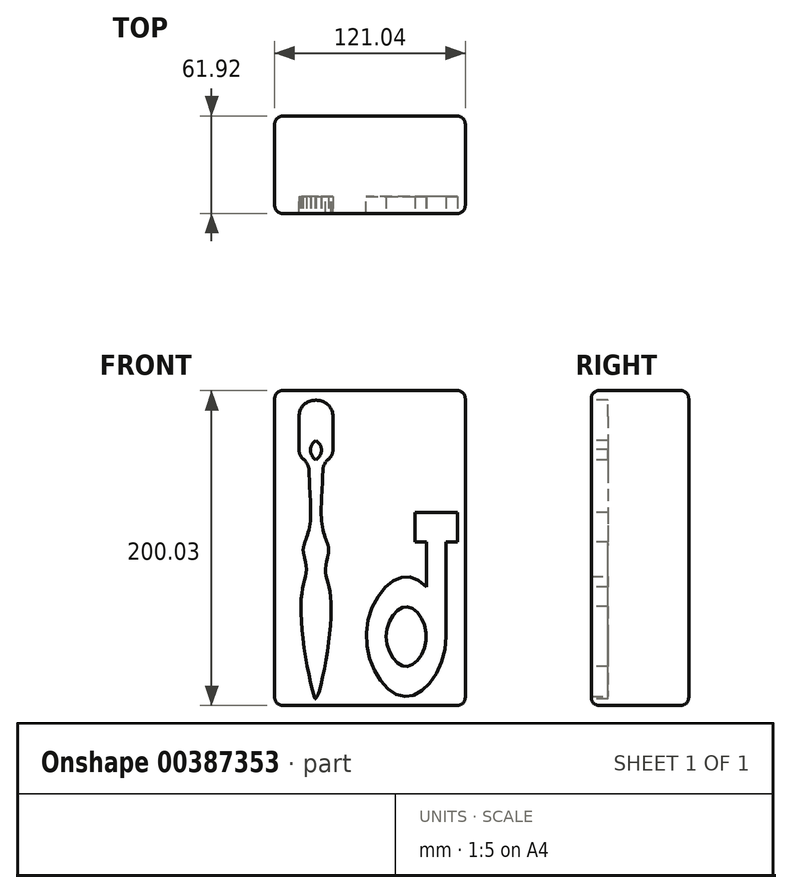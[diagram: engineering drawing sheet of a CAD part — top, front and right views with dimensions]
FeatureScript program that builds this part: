
annotation { "Feature Type Name" : "Feature", "Feature Type Description" : "" }
export const myFeature = defineFeature(function(context is Context, id is Id, definition is map)
    precondition{}
    {
        {
            var Q0;
            Q0=qCreatedBy(makeId("Top.planeOp"),FACE);
            var sketch = newSketch(context, id + "F0", { "sketchPlane" : qUnion([Q0])});
            skLineSegment(sketch, "E0.bottom", {"start": v(60.52, -30.96) * mm, "end": v(-60.52, -30.96) * mm});
            skLineSegment(sketch, "E0.top", {"start": v(60.52, 30.96) * mm, "end": v(-60.52, 30.96) * mm});
            skLineSegment(sketch, "E0.left", {"start": v(60.52, -30.96) * mm, "end": v(60.52, 30.96) * mm});
            skLineSegment(sketch, "E0.right", {"start": v(-60.52, -30.96) * mm, "end": v(-60.52, 30.96) * mm});
            skPoint(sketch, "E0.middle", {"position": v(0, 0) * mm});
            skSolve(sketch);
        }
        {
            var Q0;
            Q0=makeQuery(id+"F0.imprint","IMPRINT",FACE,{"disambiguationData":[TD([[makeQuery(id+"F0.imprint","IMPRINT",EDGE,{"derivedFrom":sQuery(id+"F0.wireOp",EDGE,"E0.bottom")}),-1.0]])]});
            extrude(context, id + "F1", {"entities" : qUnion([Q0]), "depth" : 200.02 * mm});
        }
        {
            var Q0;
            Q0=makeQuery(id+"F1.opExtrude","SWEPT_EDGE",EDGE,{"disambiguationData":[OSD([sQuery(id+"F0.wireOp",EDGE,"E0.top"),sQuery(id+"F0.wireOp",EDGE,"E0.left")])]});
            var Q1;
            Q1=makeQuery(id+"F1.opExtrude","SWEPT_EDGE",EDGE,{"disambiguationData":[OSD([sQuery(id+"F0.wireOp",EDGE,"E0.top"),sQuery(id+"F0.wireOp",EDGE,"E0.right")])]});
            var Q2;
            Q2=makeQuery(id+"F1.opExtrude","CAP_EDGE",EDGE,{"disambiguationData":[OSD([sQuery(id+"F0.wireOp",EDGE,"E0.top")])],"isStart":false});
            var Q3;
            Q3=makeQuery(id+"F1.opExtrude","CAP_EDGE",EDGE,{"disambiguationData":[OSD([sQuery(id+"F0.wireOp",EDGE,"E0.top")])],"isStart":true});
            var Q4;
            Q4=makeQuery(id+"F1.opExtrude","CAP_EDGE",EDGE,{"disambiguationData":[OSD([sQuery(id+"F0.wireOp",EDGE,"E0.right")])],"isStart":true});
            var Q5;
            Q5=makeQuery(id+"F1.opExtrude","CAP_EDGE",EDGE,{"disambiguationData":[OSD([sQuery(id+"F0.wireOp",EDGE,"E0.bottom")])],"isStart":true});
            var Q6;
            Q6=makeQuery(id+"F1.opExtrude","CAP_EDGE",EDGE,{"disambiguationData":[OSD([sQuery(id+"F0.wireOp",EDGE,"E0.left")])],"isStart":true});
            var Q7;
            Q7=makeQuery(id+"F1.opExtrude","SWEPT_EDGE",EDGE,{"disambiguationData":[OSD([sQuery(id+"F0.wireOp",EDGE,"E0.bottom"),sQuery(id+"F0.wireOp",EDGE,"E0.right")])]});
            var Q8;
            Q8=makeQuery(id+"F1.opExtrude","CAP_EDGE",EDGE,{"disambiguationData":[OSD([sQuery(id+"F0.wireOp",EDGE,"E0.right")])],"isStart":false});
            var Q9;
            Q9=makeQuery(id+"F1.opExtrude","CAP_EDGE",EDGE,{"disambiguationData":[OSD([sQuery(id+"F0.wireOp",EDGE,"E0.bottom")])],"isStart":false});
            var Q10;
            Q10=makeQuery(id+"F1.opExtrude","CAP_EDGE",EDGE,{"disambiguationData":[OSD([sQuery(id+"F0.wireOp",EDGE,"E0.left")])],"isStart":false});
            var Q11;
            Q11=makeQuery(id+"F1.opExtrude","SWEPT_EDGE",EDGE,{"disambiguationData":[OSD([sQuery(id+"F0.wireOp",EDGE,"E0.bottom"),sQuery(id+"F0.wireOp",EDGE,"E0.left")])]});
            fillet(context, id + "F2", {"entities" : qUnion([Q0, Q1, Q2, Q3, Q4, Q5, Q6, Q7, Q8, Q9, Q10, Q11]), "radius" : 5.08 * mm, "tangentPropagation" : true, "allowEdgeOverflow" : false});
        }
        {
            var Q0;
            Q0=makeQuery(id+"F1.opExtrude","SWEPT_FACE",FACE,{"disambiguationData":[OSD([sQuery(id+"F0.wireOp",EDGE,"E0.bottom")])]});
            var sketch = newSketch(context, id + "F3", { "sketchPlane" : qUnion([Q0])});
            skLineSegment(sketch, "E1", {"start": v(22.99, 43.76) * mm, "end": v(22.99, 81.86) * mm, "construction": true});
            skLineSegment(sketch, "E2", {"start": v(22.99, 43.76) * mm, "end": v(22.99, 5.66) * mm, "construction": true});
            skLineSegment(sketch, "E3", {"start": v(22.99, 43.76) * mm, "end": v(48.39, 43.76) * mm, "construction": true});
            skLineSegment(sketch, "E4", {"start": v(22.99, 43.76) * mm, "end": v(-2.41, 43.76) * mm, "construction": true});
            skFitSpline(sketch, "E5", {"points": [v(22.99, 5.66) * mm, v(-2.41, 43.76) * mm, v(22.99, 81.86) * mm, v(48.39, 43.76) * mm, v(22.99, 5.66) * mm]});
            skLineSegment(sketch, "E6", {"start": v(48.39, 43.76) * mm, "end": v(48.39, 103.81) * mm});
            skLineSegment(sketch, "E7", {"start": v(36, 75.46) * mm, "end": v(36, 103.81) * mm});
            skLineSegment(sketch, "E8", {"start": v(48.39, 103.81) * mm, "end": v(55.44, 103.81) * mm});
            skLineSegment(sketch, "E9", {"start": v(55.44, 103.81) * mm, "end": v(55.44, 122.75) * mm});
            skLineSegment(sketch, "E10", {"start": v(55.44, 122.75) * mm, "end": v(28.53, 122.75) * mm});
            skLineSegment(sketch, "E11", {"start": v(28.53, 122.75) * mm, "end": v(28.53, 103.81) * mm});
            skLineSegment(sketch, "E12", {"start": v(28.53, 103.81) * mm, "end": v(36, 103.81) * mm});
            skFitSpline(sketch, "E13", {"points": [v(10.29, 43.76) * mm, v(22.99, 62.8) * mm, v(35.69, 43.76) * mm, v(22.99, 24.7) * mm, v(10.29, 43.76) * mm]});
            skSolve(sketch);
        }
        {
            var Q0;
            Q0=makeQuery(id+"F3.imprint","IMPRINT",FACE,{"disambiguationData":[TD([[makeQuery(id+"F3.imprint","IMPRINT",EDGE,{"derivedFrom":sQuery(id+"F3.wireOp",EDGE,"E5")}),-1.0]])]});
            var sketch = newSketch(context, id + "F4", { "sketchPlane" : qUnion([Q0])});
            skLineSegment(sketch, "E14.left", {"start": v(-45.06, 189.74) * mm, "end": v(-45.06, 162.78) * mm});
            skLineSegment(sketch, "E15", {"start": v(-34.31, 195) * mm, "end": v(-34.31, 0) * mm, "construction": true});
            skPoint(sketch, "E16", {"position": v(-34.31, 166.9) * mm});
            skArc(sketch, "E17", {"start": v(-34.31, 193.9) * mm, "mid": v(-40.08, 192.83) * mm, "end": v(-45.06, 189.74) * mm});
            skPoint(sketch, "E18", {"position": v(-45.06, 189.74) * mm});
            skPoint(sketch, "E19", {"position": v(-23.56, 189.74) * mm});
            skPoint(sketch, "E20", {"position": v(-80.03, 214.85) * mm});
            skPoint(sketch, "E14.bottom.start.orphan", {"position": v(-45.06, 195) * mm});
            skArc(sketch, "E21", {"start": v(-45.06, 162.78) * mm, "mid": v(-33.6, 156.6) * mm, "end": v(-36.72, 169.25) * mm});
            skPoint(sketch, "E22.orphan", {"position": v(-45.06, 166.9) * mm});
            skPoint(sketch, "E23.orphan", {"position": v(-23.56, 166.9) * mm});
            skPoint(sketch, "E24.orphan", {"position": v(-23.56, 195) * mm});
            skLineSegment(sketch, "E25", {"start": v(-42.7, 98.32) * mm, "end": v(-42.7, 98.32) * mm});
            skLineSegment(sketch, "E26", {"start": v(-26.06, 67.88) * mm, "end": v(-26.06, 67.88) * mm});
            skFitSpline(sketch, "E27.MirrorCS", {"points": [v(-34.88, 4.14) * mm, v(-43.7, 67.88) * mm, v(-40.42, 85.52) * mm, v(-42.7, 98.32) * mm], "startDerivative": vector(-31.6, 98.95) * mm, "endDerivative": vector(-13.68, 49.84) * mm});
            skFitSpline(sketch, "E28", {"points": [v(-36.72, 169.25) * mm, v(-37.97, 116.35) * mm, v(-42.7, 98.32) * mm], "startDerivative": vector(-21.47, -88.4) * mm, "endDerivative": vector(-3.98, -35.27) * mm});
            skLineSegment(sketch, "E29.trimOffspring", {"start": v(-40.19, 26.46) * mm, "end": v(-40.19, 26.46) * mm});
            skPoint(sketch, "E30.orphan", {"position": v(-40.42, 4.14) * mm});
            skPoint(sketch, "E31.end.orphan", {"position": v(-28.2, 4.14) * mm});
            skLineSegment(sketch, "E32.trimOffspring", {"start": v(-43.7, 67.88) * mm, "end": v(-43.7, 67.88) * mm});
            skPoint(sketch, "E14.right.end.orphan", {"position": v(-23.56, 162.78) * mm});
            skFitSpline(sketch, "E33.MirrorCS", {"points": [v(-33.74, 4.14) * mm, v(-24.92, 67.88) * mm, v(-28.2, 85.52) * mm, v(-25.93, 98.32) * mm], "startDerivative": vector(31.6, 98.95) * mm, "endDerivative": vector(13.68, 49.84) * mm});
            skFitSpline(sketch, "E34.MirrorCS", {"points": [v(-31.9, 169.25) * mm, v(-30.65, 116.35) * mm, v(-25.93, 98.32) * mm], "startDerivative": vector(21.47, -88.4) * mm, "endDerivative": vector(3.98, -35.27) * mm});
            skArc(sketch, "E35.MirrorCS", {"start": v(-23.56, 162.78) * mm, "mid": v(-35.03, 156.6) * mm, "end": v(-31.9, 169.25) * mm});
            skArc(sketch, "E36.MirrorCS", {"start": v(-34.31, 193.9) * mm, "mid": v(-28.55, 192.83) * mm, "end": v(-23.56, 189.74) * mm});
            skLineSegment(sketch, "E37.MirrorCS", {"start": v(-23.56, 189.74) * mm, "end": v(-23.56, 162.78) * mm});
            skArc(sketch, "E38.trimOffspring", {"start": v(-34.31, 168.36) * mm, "mid": v(-35.48, 168.92) * mm, "end": v(-36.72, 169.25) * mm});
            skArc(sketch, "E39.trimOffspring", {"start": v(-34.31, 168.36) * mm, "mid": v(-33.15, 168.92) * mm, "end": v(-31.9, 169.25) * mm});
            skArc(sketch, "E40.trimOffspring", {"start": v(-34.31, 156.12) * mm, "mid": v(-30.95, 163.52) * mm, "end": v(-36.72, 169.25) * mm});
            skPoint(sketch, "E41", {"position": v(-38.64, 155.04) * mm});
            skPoint(sketch, "E42", {"position": v(-34.31, 3.07) * mm});
            skLineSegment(sketch, "E43", {"start": v(-34.88, 4.14) * mm, "end": v(-33.74, 4.14) * mm});
            skSolve(sketch);
        }
        {
            var Q0;
            Q0 = qSketchRegion(id + "F4", true);
            var Q1;
            {var subQ0=sQuery(id+"F4.wireOp",EDGE,"E40.trimOffspring");var subQ1=sQuery(id+"F4.wireOp",EDGE,"E35.MirrorCS");var subQ2=makeQuery(id+"F4.imprint","INTERSECT",VERTEX,{"derivedFrom":[sQuery(id+"F4.wireOp",EDGE,"E21"),subQ1,subQ0]});Q1=makeQuery(id+"F4.imprint","IMPRINT",FACE,{"disambiguationData":[TD([[makeQuery(id+"F4.imprint","IMPRINT",EDGE,{"disambiguationData":[TD([[subQ2,-1.0]])],"derivedFrom":subQ1}),-1.0]])]});}
            var Q2;
            Q2 = qSketchRegion(id + "F3", true);
            var Q3;
            Q3=sQuery(id+"F4.wireOp",EDGE,"E34.MirrorCS");
            var Q4;
            Q4=sQuery(id+"F4.wireOp",EDGE,"E28");
            var Q5;
            Q5=sQuery(id+"F4.wireOp",EDGE,"E27.MirrorCS");
            var Q6;
            Q6=sQuery(id+"F4.wireOp",EDGE,"E33.MirrorCS");
            var Q7;
            Q7=sQuery(id+"F4.wireOp",EDGE,"E37.MirrorCS");
            var Q8;
            Q8=sQuery(id+"F4.wireOp",EDGE,"E35.MirrorCS");
            var Q9;
            Q9=sQuery(id+"F4.wireOp",EDGE,"E21");
            var Q10;
            Q10=sQuery(id+"F4.wireOp",EDGE,"E14.left");
            var Q11;
            Q11=sQuery(id+"F4.wireOp",EDGE,"E17");
            var Q12;
            Q12=sQuery(id+"F4.wireOp",EDGE,"E36.MirrorCS");
            extrude(context, id + "F5", {"entities" : qUnion([Q0, Q1, Q2]), "operationType" : NewBodyOperationType.REMOVE, "surfaceEntities" : qUnion([Q3, Q4, Q5, Q6, Q7, Q8, Q9, Q10, Q11, Q12]), "oppositeDirection" : true, "depth" : 10.67 * mm});
        }
        {
            var Q0;
            Q0=makeQuery(id+"F5.boolean.opBoolean","COPY",EDGE,{"derivedFrom":makeQuery(id+"F5.opExtrude","SWEPT_EDGE",EDGE,{"disambiguationData":[OSD([sQuery(id+"F4.wireOp",EDGE,"E36.MirrorCS"),sQuery(id+"F4.wireOp",EDGE,"E37.MirrorCS")])]})});
            var Q1;
            Q1=makeQuery(id+"F5.boolean.opBoolean","COPY",EDGE,{"derivedFrom":makeQuery(id+"F5.opExtrude","SWEPT_EDGE",EDGE,{"disambiguationData":[OSD([sQuery(id+"F4.wireOp",EDGE,"E35.MirrorCS"),sQuery(id+"F4.wireOp",EDGE,"E37.MirrorCS")])]})});
            var Q2;
            Q2=makeQuery(id+"F5.boolean.opBoolean","COPY",EDGE,{"derivedFrom":makeQuery(id+"F5.opExtrude","SWEPT_EDGE",EDGE,{"disambiguationData":[OSD([sQuery(id+"F4.wireOp",EDGE,"E14.left"),sQuery(id+"F4.wireOp",EDGE,"E17")])]})});
            var Q3;
            Q3=makeQuery(id+"F5.boolean.opBoolean","COPY",EDGE,{"derivedFrom":makeQuery(id+"F5.opExtrude","SWEPT_EDGE",EDGE,{"disambiguationData":[OSD([sQuery(id+"F4.wireOp",EDGE,"E21"),sQuery(id+"F4.wireOp",EDGE,"E28")])]})});
            var Q4;
            Q4=makeQuery(id+"F5.boolean.opBoolean","COPY",EDGE,{"derivedFrom":makeQuery(id+"F5.opExtrude","SWEPT_EDGE",EDGE,{"disambiguationData":[OSD([sQuery(id+"F4.wireOp",EDGE,"E34.MirrorCS"),sQuery(id+"F4.wireOp",EDGE,"E35.MirrorCS")])]})});
            var Q5;
            Q5=makeQuery(id+"F5.boolean.opBoolean","COPY",EDGE,{"derivedFrom":makeQuery(id+"F5.opExtrude","SWEPT_EDGE",EDGE,{"disambiguationData":[OSD([sQuery(id+"F4.wireOp",EDGE,"E33.MirrorCS"),sQuery(id+"F4.wireOp",EDGE,"E34.MirrorCS")])]})});
            var Q6;
            Q6=makeQuery(id+"F5.boolean.opBoolean","COPY",EDGE,{"derivedFrom":makeQuery(id+"F5.opExtrude","SWEPT_EDGE",EDGE,{"disambiguationData":[OSD([sQuery(id+"F4.wireOp",EDGE,"E27.MirrorCS"),sQuery(id+"F4.wireOp",EDGE,"E28")])]})});
            var Q7;
            Q7=makeQuery(id+"F5.boolean.opBoolean","COPY",EDGE,{"derivedFrom":makeQuery(id+"F5.opExtrude","SWEPT_EDGE",EDGE,{"disambiguationData":[OSD([sQuery(id+"F4.wireOp",EDGE,"E33.MirrorCS"),sQuery(id+"F4.wireOp",EDGE,"E43")])]})});
            fillet(context, id + "F6", {"entities" : qUnion([Q0, Q1, Q2, Q3, Q4, Q5, Q6, Q7]), "radius" : 10.16 * mm, "tangentPropagation" : true, "allowEdgeOverflow" : false});
        }
    });
